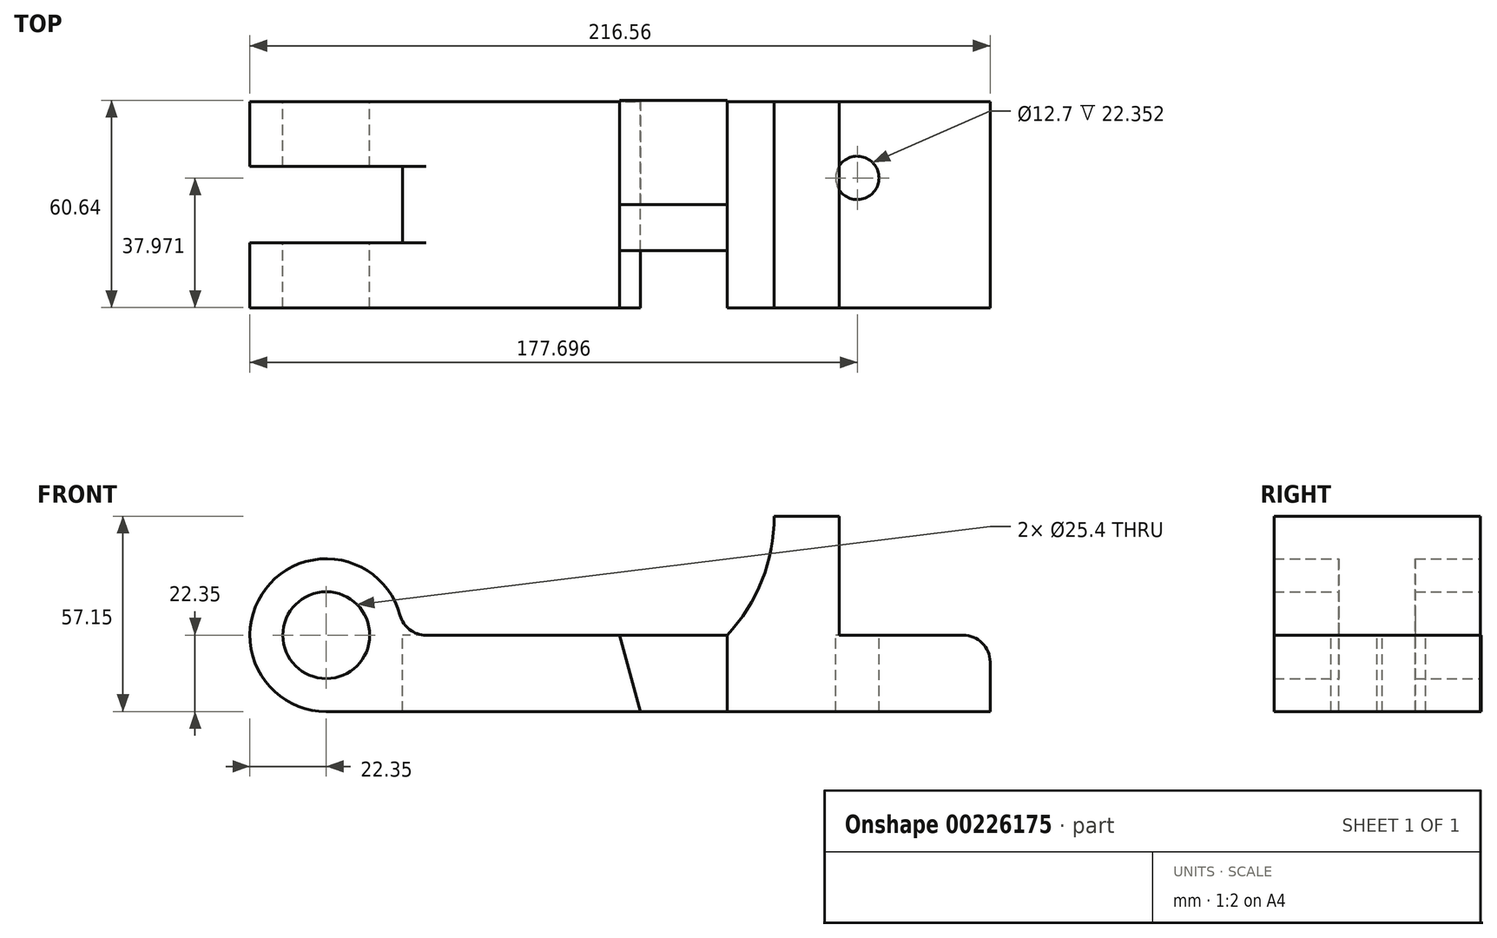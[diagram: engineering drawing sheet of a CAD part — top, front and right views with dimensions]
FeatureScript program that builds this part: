
annotation { "Feature Type Name" : "Feature", "Feature Type Description" : "" }
export const myFeature = defineFeature(function(context is Context, id is Id, definition is map)
    precondition{}
    {
        {
            var Q0;
            Q0=qCreatedBy(makeId("Front.planeOp"),FACE);
            var sketch = newSketch(context, id + "F0", { "sketchPlane" : qUnion([Q0])});
            skCircle(sketch, "E0", {"center": v(0, 0) * mm, "radius": 12.7 * mm});
            skArc(sketch, "E1", {"start": v(22.35, 0) * mm, "mid": v(-15.8, 15.8) * mm, "end": v(0, -22.35) * mm});
            skLineSegment(sketch, "E2", {"start": v(0, -22.35) * mm, "end": v(194.2, -22.35) * mm});
            skLineSegment(sketch, "E3", {"start": v(0, -22.35) * mm, "end": v(91.85, -22.35) * mm});
            skLineSegment(sketch, "E4", {"start": v(22.35, 0) * mm, "end": v(194.2, 0) * mm});
            skLineSegment(sketch, "E5", {"start": v(194.2, 0) * mm, "end": v(194.2, -22.35) * mm});
            skLineSegment(sketch, "E6", {"start": v(0, 0) * mm, "end": v(85.85, 0) * mm});
            skLineSegment(sketch, "E7", {"start": v(85.85, 0) * mm, "end": v(117.25, 0) * mm});
            skLineSegment(sketch, "E8", {"start": v(108.28, 0) * mm, "end": v(117.25, 0) * mm});
            skLineSegment(sketch, "E9", {"start": v(0, 0) * mm, "end": v(150.09, 0) * mm});
            skLineSegment(sketch, "E10", {"start": v(150.09, 0) * mm, "end": v(150.09, 34.8) * mm});
            skLineSegment(sketch, "E11", {"start": v(150.09, 34.8) * mm, "end": v(131.04, 34.8) * mm});
            skLineSegment(sketch, "E12", {"start": v(131.04, 34.8) * mm, "end": v(80.24, 34.8) * mm, "construction": true});
            skArc(sketch, "E13", {"start": v(131.04, 34.8) * mm, "mid": v(127.47, 16.08) * mm, "end": v(117.25, 0) * mm});
            skLineSegment(sketch, "E14", {"start": v(117.25, 0) * mm, "end": v(117.25, -22.35) * mm});
            skLineSegment(sketch, "E15", {"start": v(22.35, 0) * mm, "end": v(22.35, -22.35) * mm});
            skLineSegment(sketch, "E16", {"start": v(91.85, -22.35) * mm, "end": v(85.85, 0) * mm});
            skSolve(sketch);
        }
        {
            var Q0;
            {var subQ2=sQuery(id+"F0.wireOp",EDGE,"E15");Q0=makeQuery(id+"F0.imprint","IMPRINT",FACE,{"disambiguationData":[TD([[makeQuery(id+"F0.imprint","IMPRINT",EDGE,{"derivedFrom":subQ2}),1.0]])]});}
            var Q1;
            Q1=makeQuery(id+"F0.imprint","IMPRINT",FACE,{"disambiguationData":[TD([[makeQuery(id+"F0.imprint","IMPRINT",EDGE,{"derivedFrom":sQuery(id+"F0.wireOp",EDGE,"E0")}),-1.0]])]});
            var Q2;
            {var subQ1=sQuery(id+"F0.wireOp",EDGE,"E4");Q2=makeQuery(id+"F0.imprint","IMPRINT",FACE,{"disambiguationData":[TD([[makeQuery(id+"F0.imprint","IMPRINT",EDGE,{"derivedFrom":subQ1}),-1.0]])]});}
            var Q3;
            {var subQ0=sQuery(id+"F0.wireOp",EDGE,"E10");Q3=makeQuery(id+"F0.imprint","IMPRINT",FACE,{"disambiguationData":[TD([[makeQuery(id+"F0.imprint","IMPRINT",EDGE,{"derivedFrom":subQ0}),1.0]])]});}
            extrude(context, id + "F1", {"entities" : qUnion([Q0, Q1, Q2, Q3]), "endBound" : BoundingType.SYMMETRIC, "depth" : 60.32 * mm});
        }
        {
            var Q0;
            Q0=makeQuery(id+"F1.opExtrude","SWEPT_FACE",FACE,{"disambiguationData":[OSD([sQuery(id+"F0.wireOp",EDGE,"E4"),sQuery(id+"F0.wireOp",EDGE,"E9")])]});
            var sketch = newSketch(context, id + "F2", { "sketchPlane" : qUnion([Q0])});
            skCircle(sketch, "E17", {"center": v(155.35, 7.81) * mm, "radius": 6.35 * mm});
            skLineSegment(sketch, "E18", {"start": v(22.35, -11.16) * mm, "end": v(-32.17, -11.16) * mm});
            skLineSegment(sketch, "E19", {"start": v(-32.17, -11.16) * mm, "end": v(-32.17, 11.16) * mm});
            skLineSegment(sketch, "E20", {"start": v(-32.17, 11.16) * mm, "end": v(22.35, 11.16) * mm});
            skSolve(sketch);
        }
        {
            var Q0;
            Q0=makeQuery(id+"F2.imprint","IMPRINT",FACE,{"disambiguationData":[TD([[makeQuery(id+"F2.imprint","IMPRINT",EDGE,{"derivedFrom":sQuery(id+"F2.wireOp",EDGE,"E17")}),1.0]])]});
            extrude(context, id + "F3", {"entities" : qUnion([Q0]), "operationType" : NewBodyOperationType.REMOVE, "endBound" : BoundingType.THROUGH_ALL, "oppositeDirection" : true, "depth" : 25.4 * mm});
        }
        {
            var Q0;
            {var subQ0=sQuery(id+"F2.wireOp",EDGE,"E18");Q0=makeQuery(id+"F2.imprint","IMPRINT",FACE,{"disambiguationData":[TD([[makeQuery(id+"F2.imprint","IMPRINT",EDGE,{"derivedFrom":subQ0}),-1.0]])]});}
            extrude(context, id + "F4", {"entities" : qUnion([Q0]), "operationType" : NewBodyOperationType.REMOVE, "endBound" : BoundingType.SYMMETRIC, "oppositeDirection" : true, "depth" : 127 * mm});
        }
        {
            var Q0;
            {var subQ0=sQuery(id+"F0.wireOp",EDGE,"E10");Q0=makeQuery(id+"F0.imprint","IMPRINT",FACE,{"disambiguationData":[TD([[makeQuery(id+"F0.imprint","IMPRINT",EDGE,{"derivedFrom":subQ0}),1.0]])]});}
            extrude(context, id + "F5", {"entities" : qUnion([Q0]), "operationType" : NewBodyOperationType.ADD, "endBound" : BoundingType.SYMMETRIC, "depth" : 60.32 * mm});
        }
        {
            var Q0;
            {var subQ0=sQuery(id+"F0.wireOp",EDGE,"E9");var subQ1=sQuery(id+"F0.wireOp",EDGE,"E4");var subQ2=sQuery(id+"F0.wireOp",EDGE,"E1");var subQ3=sQuery(id+"F0.wireOp",EDGE,"E15");Q0=makeQuery(id+"F4.boolean.opBoolean","SPLIT",EDGE,{"disambiguationData":[TD([makeQuery(id+"F1.opExtrude","CAP_FACE",FACE,{"disambiguationData":[OSD([sQuery(id+"F0.wireOp",EDGE,"E0"),subQ2,sQuery(id+"F0.wireOp",EDGE,"E2"),sQuery(id+"F0.wireOp",EDGE,"E3"),subQ1,sQuery(id+"F0.wireOp",EDGE,"E5"),subQ0])],"isStart":false}),makeQuery(id+"F1.opExtrude","SWEPT_FACE",FACE,{"disambiguationData":[OSD([subQ2])]}),makeQuery(id+"F1.opExtrude","SWEPT_FACE",FACE,{"disambiguationData":[OSD([subQ1,subQ0])]}),makeQuery(id+"F4.opExtrude","SWEPT_FACE",FACE,{"disambiguationData":[OSD([sQuery(id+"F2.wireOp",EDGE,"E18")])]}),makeQuery(id+"F4.opExtrude","SWEPT_FACE",FACE,{"disambiguationData":[OSD([subQ2,subQ0,subQ3])]})])],"derivedFrom":makeQuery(id+"F1.opExtrude","SWEPT_EDGE",EDGE,{"disambiguationData":[OSD([subQ2,subQ0,subQ3])]})});}
            var Q1;
            {var subQ0=sQuery(id+"F0.wireOp",EDGE,"E9");var subQ1=sQuery(id+"F0.wireOp",EDGE,"E4");var subQ2=sQuery(id+"F0.wireOp",EDGE,"E1");var subQ3=sQuery(id+"F0.wireOp",EDGE,"E15");Q1=makeQuery(id+"F4.boolean.opBoolean","SPLIT",EDGE,{"disambiguationData":[TD([makeQuery(id+"F1.opExtrude","CAP_FACE",FACE,{"disambiguationData":[OSD([sQuery(id+"F0.wireOp",EDGE,"E0"),subQ2,sQuery(id+"F0.wireOp",EDGE,"E2"),sQuery(id+"F0.wireOp",EDGE,"E3"),subQ1,sQuery(id+"F0.wireOp",EDGE,"E5"),subQ0])],"isStart":true}),makeQuery(id+"F1.opExtrude","SWEPT_FACE",FACE,{"disambiguationData":[OSD([subQ2])]}),makeQuery(id+"F1.opExtrude","SWEPT_FACE",FACE,{"disambiguationData":[OSD([subQ1,subQ0])]}),makeQuery(id+"F4.opExtrude","SWEPT_FACE",FACE,{"disambiguationData":[OSD([sQuery(id+"F2.wireOp",EDGE,"E20")])]}),makeQuery(id+"F4.opExtrude","SWEPT_FACE",FACE,{"disambiguationData":[OSD([subQ2,subQ0,subQ3])]})])],"derivedFrom":makeQuery(id+"F1.opExtrude","SWEPT_EDGE",EDGE,{"disambiguationData":[OSD([subQ2,subQ0,subQ3])]})});}
            fillet(context, id + "F6", {"entities" : qUnion([Q0, Q1]), "radius" : 7.87 * mm, "tangentPropagation" : true, "allowEdgeOverflow" : false});
        }
        {
            var Q0;
            {var subQ2=sQuery(id+"F0.wireOp",EDGE,"E14");Q0=makeQuery(id+"F0.imprint","IMPRINT",FACE,{"disambiguationData":[TD([[makeQuery(id+"F0.imprint","IMPRINT",EDGE,{"derivedFrom":subQ2}),-1.0]])]});}
            extrude(context, id + "F7", {"entities" : qUnion([Q0]), "oppositeDirection" : true, "depth" : 30.48 * mm});
        }
        {
            var Q0;
            {var subQ2=sQuery(id+"F0.wireOp",EDGE,"E14");Q0=makeQuery(id+"F0.imprint","IMPRINT",FACE,{"disambiguationData":[TD([[makeQuery(id+"F0.imprint","IMPRINT",EDGE,{"derivedFrom":subQ2}),-1.0]])]});}
            extrude(context, id + "F8", {"entities" : qUnion([Q0]), "depth" : 13.46 * mm});
        }
        {
            var Q0;
            {var subQ0=sQuery(id+"F2.wireOp",EDGE,"E17");var subQ1=makeQuery(id+"F1.opExtrude","SWEPT_EDGE",EDGE,{"disambiguationData":[OSD([sQuery(id+"F0.wireOp",EDGE,"E4"),sQuery(id+"F0.wireOp",EDGE,"E9"),sQuery(id+"F0.wireOp",EDGE,"E10")])]});var subQ2=makeQuery(id+"F2.imprint","INTERSECT",VERTEX,{"disambiguationData":[OD(0.0)],"derivedFrom":[subQ1,subQ0]});Q0=makeQuery(id+"F2.imprint","IMPRINT",FACE,{"disambiguationData":[TD([[makeQuery(id+"F2.imprint","IMPRINT",EDGE,{"disambiguationData":[TD([[subQ2,1.0]])],"derivedFrom":subQ0}),1.0]])]});}
            extrude(context, id + "F9", {"entities" : qUnion([Q0]), "operationType" : NewBodyOperationType.REMOVE, "oppositeDirection" : true, "depth" : 25.4 * mm});
        }
        {
            var Q0;
            Q0=makeQuery(id+"F1.opExtrude","SWEPT_EDGE",EDGE,{"disambiguationData":[OSD([sQuery(id+"F0.wireOp",EDGE,"E4"),sQuery(id+"F0.wireOp",EDGE,"E5")])]});
            fillet(context, id + "F10", {"entities" : qUnion([Q0]), "radius" : 7.87 * mm, "tangentPropagation" : true, "allowEdgeOverflow" : false});
        }
    });
